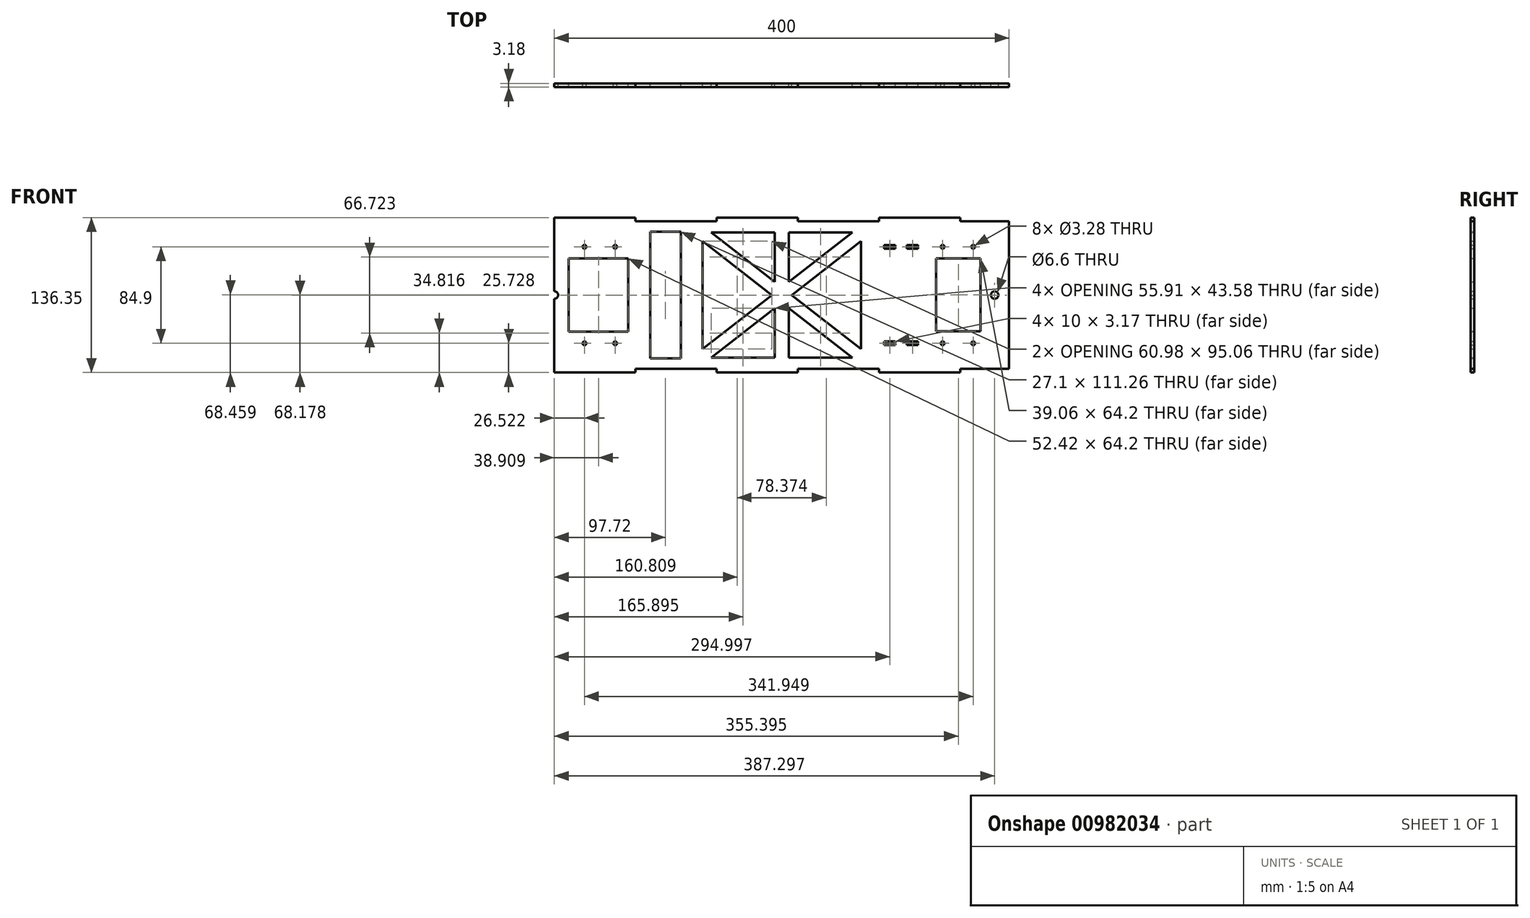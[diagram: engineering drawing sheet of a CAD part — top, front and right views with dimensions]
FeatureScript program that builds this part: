
annotation { "Feature Type Name" : "Feature", "Feature Type Description" : "" }
export const myFeature = defineFeature(function(context is Context, id is Id, definition is map)
    precondition{}
    {
        {
            var Q0;
            Q0=qCreatedBy(makeId("Front.planeOp"),FACE);
            var sketch = newSketch(context, id + "F0", { "sketchPlane" : qUnion([Q0])});
            skLineSegment(sketch, "E0.bottom", {"start": v(122.16, -50.2) * mm, "end": v(-277.84, -50.2) * mm, "construction": true});
            skLineSegment(sketch, "E0.top", {"start": v(122.16, 79.8) * mm, "end": v(-277.84, 79.8) * mm, "construction": true});
            skLineSegment(sketch, "E0.left", {"start": v(122.16, -50.2) * mm, "end": v(122.16, 79.8) * mm});
            skLineSegment(sketch, "E0.right", {"start": v(-277.84, -50.2) * mm, "end": v(-277.84, 79.8) * mm});
            skCircle(sketch, "E1", {"center": v(-237.84, 57.25) * mm, "radius": 4 * mm, "construction": true});
            skLineSegment(sketch, "E2", {"start": v(-237.84, 57.25) * mm, "end": v(-233.84, 57.25) * mm, "construction": true});
            skLineSegment(sketch, "E3", {"start": v(-237.84, 57.25) * mm, "end": v(-237.84, 61.25) * mm, "construction": true});
            skCircle(sketch, "E4", {"center": v(-224.37, 57.25) * mm, "radius": 1.64 * mm});
            skCircle(sketch, "E5.MirrorC", {"center": v(-251.32, 57.25) * mm, "radius": 1.64 * mm});
            skCircle(sketch, "E6", {"center": v(-237.84, -27.65) * mm, "radius": 4 * mm, "construction": true});
            skLineSegment(sketch, "E7", {"start": v(-237.84, -27.65) * mm, "end": v(-233.84, -27.65) * mm, "construction": true});
            skLineSegment(sketch, "E8", {"start": v(-237.84, -27.65) * mm, "end": v(-237.84, -23.65) * mm, "construction": true});
            skCircle(sketch, "E9", {"center": v(-224.37, -27.65) * mm, "radius": 1.64 * mm});
            skCircle(sketch, "E10.MirrorC", {"center": v(-251.32, -27.65) * mm, "radius": 1.64 * mm});
            skCircle(sketch, "E11", {"center": v(77.16, -27.65) * mm, "radius": 4 * mm, "construction": true});
            skLineSegment(sketch, "E12", {"start": v(77.16, -27.65) * mm, "end": v(81.16, -27.65) * mm, "construction": true});
            skLineSegment(sketch, "E13", {"start": v(77.16, -27.65) * mm, "end": v(77.16, -23.65) * mm, "construction": true});
            skCircle(sketch, "E14", {"center": v(90.63, -27.65) * mm, "radius": 1.64 * mm});
            skCircle(sketch, "E15.MirrorC", {"center": v(63.68, -27.65) * mm, "radius": 1.64 * mm});
            skCircle(sketch, "E16", {"center": v(77.16, 57.25) * mm, "radius": 4 * mm, "construction": true});
            skLineSegment(sketch, "E17", {"start": v(77.16, 57.25) * mm, "end": v(81.16, 57.25) * mm, "construction": true});
            skLineSegment(sketch, "E18", {"start": v(77.16, 57.25) * mm, "end": v(77.16, 61.25) * mm, "construction": true});
            skCircle(sketch, "E19", {"center": v(90.63, 57.25) * mm, "radius": 1.64 * mm});
            skCircle(sketch, "E20.MirrorC", {"center": v(63.68, 57.25) * mm, "radius": 1.64 * mm});
            skPoint(sketch, "E21.middle.positionSnap0", {"position": v(-237.84, -25.65) * mm});
            skPoint(sketch, "E21.centerSnap0", {"position": v(-237.84, -25.65) * mm});
            skCircle(sketch, "E22", {"center": v(109.46, 14.8) * mm, "radius": 3.3 * mm});
            skLineSegment(sketch, "E23", {"start": v(-77.84, 79.8) * mm, "end": v(-77.84, -50.2) * mm, "construction": true});
            skLineSegment(sketch, "E24", {"start": v(-77.84, 14.8) * mm, "end": v(-277.84, 14.8) * mm, "construction": true});
            skLineSegment(sketch, "E25.right", {"start": v(-265.14, -17.3) * mm, "end": v(-265.14, 46.9) * mm});
            skPoint(sketch, "E25.middle", {"position": v(-196.56, 14.8) * mm});
            skLineSegment(sketch, "E26", {"start": v(-77.84, 14.8) * mm, "end": v(122.16, 14.8) * mm, "construction": true});
            skLineSegment(sketch, "E27.right", {"start": v(97.09, 47.18) * mm, "end": v(97.09, -17.02) * mm});
            skLineSegment(sketch, "E28", {"start": v(-166.57, 70.43) * mm, "end": v(-166.57, -40.83) * mm});
            skLineSegment(sketch, "E29.right", {"start": v(-212.72, 46.9) * mm, "end": v(-212.72, -17.3) * mm});
            skLineSegment(sketch, "E30", {"start": v(-265.14, 46.9) * mm, "end": v(-212.72, 46.9) * mm});
            skLineSegment(sketch, "E31", {"start": v(-265.14, -17.3) * mm, "end": v(-212.72, -17.3) * mm});
            skLineSegment(sketch, "E32.right", {"start": v(58.02, 47.18) * mm, "end": v(58.02, -17.02) * mm});
            skLineSegment(sketch, "E33", {"start": v(58.02, 47.18) * mm, "end": v(97.09, 47.18) * mm});
            skLineSegment(sketch, "E34", {"start": v(58.02, -17.02) * mm, "end": v(97.09, -17.02) * mm});
            skLineSegment(sketch, "E35.bottom", {"start": v(-8.17, -40.35) * mm, "end": v(-147.52, -40.35) * mm});
            skLineSegment(sketch, "E35.top", {"start": v(-8.17, 69.95) * mm, "end": v(-147.52, 69.95) * mm});
            skLineSegment(sketch, "E35.left", {"start": v(-8.17, -40.35) * mm, "end": v(-8.17, 69.95) * mm});
            skLineSegment(sketch, "E35.right", {"start": v(-147.52, -40.35) * mm, "end": v(-147.52, 69.95) * mm});
            skPoint(sketch, "E35.middle", {"position": v(-77.84, 14.8) * mm});
            skLineSegment(sketch, "E36", {"start": v(-147.52, 62.33) * mm, "end": v(-15.79, -40.35) * mm});
            skLineSegment(sketch, "E37", {"start": v(-139.9, 69.95) * mm, "end": v(-8.17, -32.73) * mm});
            skLineSegment(sketch, "E38.MirrorCS", {"start": v(-15.79, 69.95) * mm, "end": v(-147.52, -32.73) * mm});
            skLineSegment(sketch, "E39.MirrorCS", {"start": v(-8.17, 62.33) * mm, "end": v(-139.9, -40.35) * mm});
            skLineSegment(sketch, "E40.bottom", {"start": v(-71.7, -40.35) * mm, "end": v(-83.99, -40.35) * mm});
            skLineSegment(sketch, "E40.top", {"start": v(-71.7, 69.95) * mm, "end": v(-83.99, 69.95) * mm});
            skLineSegment(sketch, "E40.left", {"start": v(-71.7, -40.35) * mm, "end": v(-71.7, 69.95) * mm});
            skLineSegment(sketch, "E40.right", {"start": v(-83.99, -40.35) * mm, "end": v(-83.99, 69.95) * mm});
            skLineSegment(sketch, "E41", {"start": v(-193.67, 70.43) * mm, "end": v(-193.67, -40.83) * mm});
            skLineSegment(sketch, "E42", {"start": v(-193.67, 70.43) * mm, "end": v(-166.57, 70.43) * mm});
            skLineSegment(sketch, "E43", {"start": v(-193.67, -40.83) * mm, "end": v(-166.57, -40.83) * mm});
            skLineSegment(sketch, "E44.top", {"start": v(-277.84, -53.38) * mm, "end": v(-206.41, -53.38) * mm});
            skLineSegment(sketch, "E44.left", {"start": v(-277.84, -50.2) * mm, "end": v(-277.84, -53.38) * mm});
            skLineSegment(sketch, "E44.right", {"start": v(-206.41, -50.2) * mm, "end": v(-206.41, -53.38) * mm});
            skLineSegment(sketch, "E45.bottom", {"start": v(-206.41, -50.2) * mm, "end": v(-134.99, -50.2) * mm});
            skLineSegment(sketch, "E46.1.0.0", {"start": v(-134.99, -53.38) * mm, "end": v(-63.56, -53.38) * mm});
            skLineSegment(sketch, "E46.1.0.1", {"start": v(-63.56, -50.2) * mm, "end": v(7.87, -50.2) * mm});
            skLineSegment(sketch, "E46.1.0.2", {"start": v(-134.99, -50.2) * mm, "end": v(-134.99, -53.38) * mm});
            skLineSegment(sketch, "E46.1.0.3", {"start": v(-63.56, -50.2) * mm, "end": v(-63.56, -53.38) * mm});
            skLineSegment(sketch, "E46.1.0.4", {"start": v(-63.56, -50.2) * mm, "end": v(-63.56, -53.38) * mm});
            skLineSegment(sketch, "E46.2.0.0", {"start": v(7.87, -53.38) * mm, "end": v(79.3, -53.38) * mm});
            skLineSegment(sketch, "E46.2.0.2", {"start": v(7.87, -50.2) * mm, "end": v(7.87, -53.38) * mm});
            skLineSegment(sketch, "E46.direction1", {"start": v(-277.84, -53.38) * mm, "end": v(-134.99, -53.38) * mm, "construction": true});
            skLineSegment(sketch, "E47.MirrorCS", {"start": v(-63.56, 79.8) * mm, "end": v(-63.56, 82.97) * mm});
            skLineSegment(sketch, "E48.MirrorCS", {"start": v(-206.41, 79.8) * mm, "end": v(-206.41, 82.97) * mm});
            skLineSegment(sketch, "E49.MirrorCS", {"start": v(-134.99, 79.8) * mm, "end": v(-134.99, 82.97) * mm});
            skLineSegment(sketch, "E50.MirrorCS", {"start": v(-277.84, 79.8) * mm, "end": v(-277.84, 82.97) * mm});
            skLineSegment(sketch, "E51.MirrorCS", {"start": v(7.87, 79.8) * mm, "end": v(7.87, 82.97) * mm});
            skLineSegment(sketch, "E52.MirrorCS", {"start": v(-63.56, 79.8) * mm, "end": v(7.87, 79.8) * mm});
            skLineSegment(sketch, "E53.MirrorCS", {"start": v(-277.84, 82.97) * mm, "end": v(-206.41, 82.97) * mm});
            skLineSegment(sketch, "E54.MirrorCS", {"start": v(-206.41, 79.8) * mm, "end": v(-134.99, 79.8) * mm});
            skLineSegment(sketch, "E55.MirrorCS", {"start": v(7.87, 82.97) * mm, "end": v(79.3, 82.97) * mm});
            skLineSegment(sketch, "E56.MirrorCS", {"start": v(-277.84, 82.97) * mm, "end": v(-134.99, 82.97) * mm, "construction": true});
            skLineSegment(sketch, "E57.MirrorCS", {"start": v(-134.99, 82.97) * mm, "end": v(-63.56, 82.97) * mm});
            skLineSegment(sketch, "E58.MirrorCS", {"start": v(42.16, -26.06) * mm, "end": v(42.16, -29.24) * mm});
            skLineSegment(sketch, "E59.MirrorCS", {"start": v(12.16, -26.06) * mm, "end": v(12.16, -29.24) * mm});
            skCircle(sketch, "E60.MirrorC", {"center": v(27.16, -27.65) * mm, "radius": 2.35 * mm, "construction": true});
            skLineSegment(sketch, "E61.bottom", {"start": v(12.16, -26.06) * mm, "end": v(22.16, -26.06) * mm});
            skLineSegment(sketch, "E61.top", {"start": v(12.16, -29.24) * mm, "end": v(22.16, -29.24) * mm});
            skLineSegment(sketch, "E61.right", {"start": v(22.16, -26.06) * mm, "end": v(22.16, -29.24) * mm});
            skLineSegment(sketch, "E62.bottom", {"start": v(42.16, -26.06) * mm, "end": v(32.16, -26.06) * mm});
            skLineSegment(sketch, "E62.top", {"start": v(42.16, -29.24) * mm, "end": v(32.16, -29.24) * mm});
            skLineSegment(sketch, "E62.right", {"start": v(32.16, -26.06) * mm, "end": v(32.16, -29.24) * mm});
            skLineSegment(sketch, "E63.MirrorCS", {"start": v(12.16, 55.66) * mm, "end": v(12.16, 58.84) * mm});
            skLineSegment(sketch, "E64.MirrorCS", {"start": v(42.16, 55.66) * mm, "end": v(42.16, 58.84) * mm});
            skLineSegment(sketch, "E65.MirrorCS", {"start": v(12.16, 58.84) * mm, "end": v(22.16, 58.84) * mm});
            skLineSegment(sketch, "E66.MirrorCS", {"start": v(42.16, 55.66) * mm, "end": v(32.16, 55.66) * mm});
            skLineSegment(sketch, "E67.MirrorCS", {"start": v(42.16, 58.84) * mm, "end": v(32.16, 58.84) * mm});
            skCircle(sketch, "E68.MirrorC", {"center": v(27.16, 57.25) * mm, "radius": 2.35 * mm, "construction": true});
            skLineSegment(sketch, "E69.MirrorCS", {"start": v(12.16, 55.66) * mm, "end": v(22.16, 55.66) * mm});
            skLineSegment(sketch, "E70.MirrorCS", {"start": v(32.16, 55.66) * mm, "end": v(32.16, 58.84) * mm});
            skLineSegment(sketch, "E71.MirrorCS", {"start": v(22.16, 55.66) * mm, "end": v(22.16, 58.84) * mm});
            skLineSegment(sketch, "E72", {"start": v(79.3, 82.97) * mm, "end": v(79.3, 79.8) * mm});
            skLineSegment(sketch, "E73", {"start": v(79.3, 79.8) * mm, "end": v(122.16, 79.8) * mm});
            skLineSegment(sketch, "E74", {"start": v(79.3, -53.38) * mm, "end": v(79.3, -50.2) * mm});
            skLineSegment(sketch, "E75", {"start": v(79.3, -50.2) * mm, "end": v(122.16, -50.2) * mm});
            skCircle(sketch, "E76", {"center": v(-277.84, 14.8) * mm, "radius": 3.3 * mm});
            skSolve(sketch);
        }
        {
            var Q0;
            Q0=makeQuery(id+"F0.imprint","IMPRINT",FACE,{"disambiguationData":[TD([[makeQuery(id+"F0.imprint","IMPRINT",EDGE,{"derivedFrom":sQuery(id+"F0.wireOp",EDGE,"E0.left")}),1.0]])]});
            var Q1;
            {var subQ1=sQuery(id+"F0.wireOp",EDGE,"E35.top");var subQ6=sQuery(id+"F0.wireOp",EDGE,"E35.right");var subQ10=makeQuery(id+"F0.imprint","INTERSECT",VERTEX,{"derivedFrom":[subQ1,subQ6]});Q1=makeQuery(id+"F0.imprint","IMPRINT",FACE,{"disambiguationData":[TD([[makeQuery(id+"F0.imprint","IMPRINT",EDGE,{"disambiguationData":[TD([[subQ10,1.0]])],"derivedFrom":subQ1}),1.0]])]});}
            var Q2;
            {var subQ6=sQuery(id+"F0.wireOp",EDGE,"E35.top");var subQ9=sQuery(id+"F0.wireOp",EDGE,"E35.left");var subQ10=makeQuery(id+"F0.imprint","INTERSECT",VERTEX,{"derivedFrom":[subQ6,subQ9]});Q2=makeQuery(id+"F0.imprint","IMPRINT",FACE,{"disambiguationData":[TD([[makeQuery(id+"F0.imprint","IMPRINT",EDGE,{"disambiguationData":[TD([[subQ10,-1.0]])],"derivedFrom":subQ6}),1.0]])]});}
            var Q3;
            {var subQ0=sQuery(id+"F0.wireOp",EDGE,"E36");var subQ1=sQuery(id+"F0.wireOp",EDGE,"E35.bottom");var subQ2=makeQuery(id+"F0.imprint","INTERSECT",VERTEX,{"derivedFrom":[subQ1,subQ0]});Q3=makeQuery(id+"F0.imprint","IMPRINT",FACE,{"disambiguationData":[TD([[makeQuery(id+"F0.imprint","IMPRINT",EDGE,{"disambiguationData":[TD([[subQ2,1.0]])],"derivedFrom":subQ1}),-1.0]])]});}
            var Q4;
            {var subQ1=sQuery(id+"F0.wireOp",EDGE,"E35.right");var subQ7=sQuery(id+"F0.wireOp",EDGE,"E35.bottom");var subQ8=makeQuery(id+"F0.imprint","INTERSECT",VERTEX,{"derivedFrom":[subQ7,subQ1]});Q4=makeQuery(id+"F0.imprint","IMPRINT",FACE,{"disambiguationData":[TD([[makeQuery(id+"F0.imprint","IMPRINT",EDGE,{"disambiguationData":[TD([[subQ8,1.0]])],"derivedFrom":subQ7}),-1.0]])]});}
            var Q5;
            {var subQ1=sQuery(id+"F0.wireOp",EDGE,"E35.bottom");var subQ7=sQuery(id+"F0.wireOp",EDGE,"E40.right");var subQ9=makeQuery(id+"F0.imprint","INTERSECT",VERTEX,{"derivedFrom":[subQ1,subQ7]});Q5=makeQuery(id+"F0.imprint","IMPRINT",FACE,{"disambiguationData":[TD([[makeQuery(id+"F0.imprint","IMPRINT",EDGE,{"disambiguationData":[TD([[subQ9,1.0]])],"derivedFrom":subQ1}),-1.0]])]});}
            var Q6;
            {var subQ0=sQuery(id+"F0.wireOp",EDGE,"E40.left");var subQ1=sQuery(id+"F0.wireOp",EDGE,"E36");var subQ2=makeQuery(id+"F0.imprint","INTERSECT",VERTEX,{"derivedFrom":[subQ1,subQ0]});Q6=makeQuery(id+"F0.imprint","IMPRINT",FACE,{"disambiguationData":[TD([[makeQuery(id+"F0.imprint","IMPRINT",EDGE,{"disambiguationData":[TD([[subQ2,1.0]])],"derivedFrom":subQ1}),1.0]])]});}
            var Q7;
            {var subQ0=sQuery(id+"F0.wireOp",EDGE,"E40.right");var subQ1=sQuery(id+"F0.wireOp",EDGE,"E36");var subQ2=makeQuery(id+"F0.imprint","INTERSECT",VERTEX,{"derivedFrom":[subQ1,subQ0]});Q7=makeQuery(id+"F0.imprint","IMPRINT",FACE,{"disambiguationData":[TD([[makeQuery(id+"F0.imprint","IMPRINT",EDGE,{"disambiguationData":[TD([[subQ2,-1.0]])],"derivedFrom":subQ1}),-1.0]])]});}
            var Q8;
            {var subQ0=sQuery(id+"F0.wireOp",EDGE,"E40.right");var subQ1=sQuery(id+"F0.wireOp",EDGE,"E36");var subQ2=makeQuery(id+"F0.imprint","INTERSECT",VERTEX,{"derivedFrom":[subQ1,subQ0]});Q8=makeQuery(id+"F0.imprint","IMPRINT",FACE,{"disambiguationData":[TD([[makeQuery(id+"F0.imprint","IMPRINT",EDGE,{"disambiguationData":[TD([[subQ2,1.0]])],"derivedFrom":subQ1}),1.0]])]});}
            var Q9;
            {var subQ3=sQuery(id+"F0.wireOp",EDGE,"E36");var subQ9=sQuery(id+"F0.wireOp",EDGE,"E40.right");var subQ10=makeQuery(id+"F0.imprint","INTERSECT",VERTEX,{"derivedFrom":[subQ3,subQ9]});Q9=makeQuery(id+"F0.imprint","IMPRINT",FACE,{"disambiguationData":[TD([[makeQuery(id+"F0.imprint","IMPRINT",EDGE,{"disambiguationData":[TD([[subQ10,-1.0]])],"derivedFrom":subQ3}),1.0]])]});}
            var Q10;
            {var subQ0=sQuery(id+"F0.wireOp",EDGE,"E40.left");var subQ1=sQuery(id+"F0.wireOp",EDGE,"E37");var subQ2=makeQuery(id+"F0.imprint","INTERSECT",VERTEX,{"derivedFrom":[subQ1,subQ0]});Q10=makeQuery(id+"F0.imprint","IMPRINT",FACE,{"disambiguationData":[TD([[makeQuery(id+"F0.imprint","IMPRINT",EDGE,{"disambiguationData":[TD([[subQ2,1.0]])],"derivedFrom":subQ1}),1.0]])]});}
            var Q11;
            {var subQ0=sQuery(id+"F0.wireOp",EDGE,"E40.right");var subQ1=sQuery(id+"F0.wireOp",EDGE,"E37");var subQ2=makeQuery(id+"F0.imprint","INTERSECT",VERTEX,{"derivedFrom":[subQ1,subQ0]});Q11=makeQuery(id+"F0.imprint","IMPRINT",FACE,{"disambiguationData":[TD([[makeQuery(id+"F0.imprint","IMPRINT",EDGE,{"disambiguationData":[TD([[subQ2,-1.0]])],"derivedFrom":subQ1}),-1.0]])]});}
            var Q12;
            {var subQ5=sQuery(id+"F0.wireOp",EDGE,"E40.right");var subQ7=sQuery(id+"F0.wireOp",EDGE,"E35.top");var subQ9=makeQuery(id+"F0.imprint","INTERSECT",VERTEX,{"derivedFrom":[subQ7,subQ5]});Q12=makeQuery(id+"F0.imprint","IMPRINT",FACE,{"disambiguationData":[TD([[makeQuery(id+"F0.imprint","IMPRINT",EDGE,{"disambiguationData":[TD([[subQ9,1.0]])],"derivedFrom":subQ7}),1.0]])]});}
            var Q13;
            {var subQ0=sQuery(id+"F0.wireOp",EDGE,"E39.MirrorCS");var subQ1=sQuery(id+"F0.wireOp",EDGE,"E37");var subQ2=makeQuery(id+"F0.imprint","INTERSECT",VERTEX,{"derivedFrom":[subQ1,subQ0]});Q13=makeQuery(id+"F0.imprint","IMPRINT",FACE,{"disambiguationData":[TD([[makeQuery(id+"F0.imprint","IMPRINT",EDGE,{"disambiguationData":[TD([[subQ2,1.0]])],"derivedFrom":subQ1}),-1.0]])]});}
            extrude(context, id + "F1", {"entities" : qUnion([Q0, Q1, Q2, Q3, Q4, Q5, Q6, Q7, Q8, Q9, Q10, Q11, Q12, Q13]), "depth" : 3.17 * mm, "offsetDistance" : 25.4 * mm});
        }
    });
